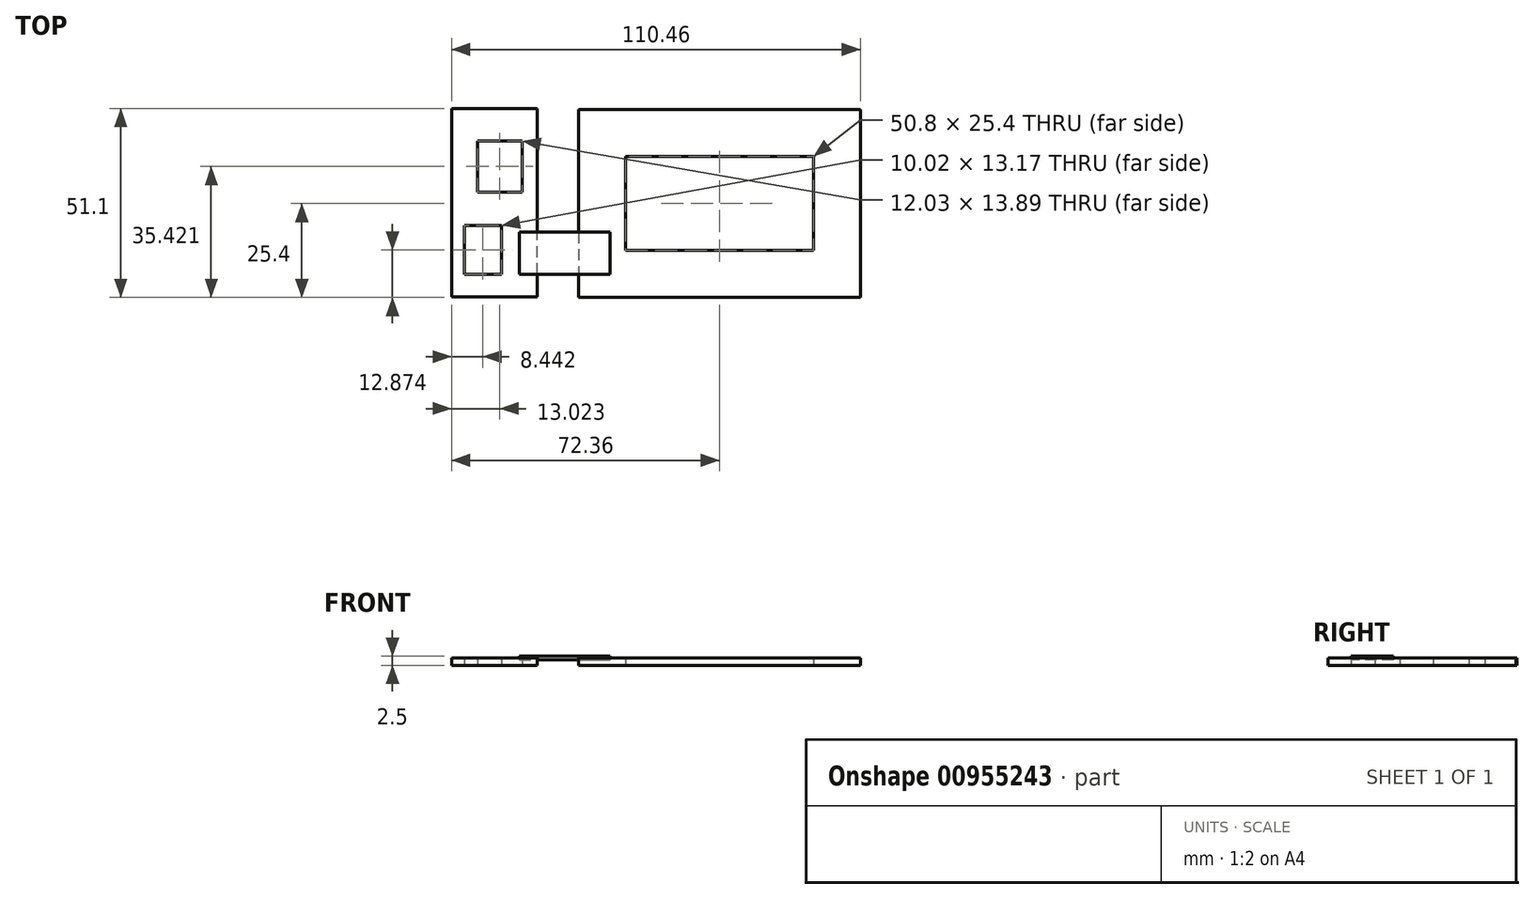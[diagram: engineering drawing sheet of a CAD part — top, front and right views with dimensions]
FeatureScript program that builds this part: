
annotation { "Feature Type Name" : "Feature", "Feature Type Description" : "" }
export const myFeature = defineFeature(function(context is Context, id is Id, definition is map)
    precondition{}
    {
        {
            var Q0;
            Q0=qCreatedBy(makeId("Top.planeOp"),FACE);
            var sketch = newSketch(context, id + "F0", { "sketchPlane" : qUnion([Q0])});
            skLineSegment(sketch, "E0.bottom", {"start": v(-38.1, 25.4) * mm, "end": v(38.1, 25.4) * mm});
            skLineSegment(sketch, "E0.top", {"start": v(-38.1, -25.4) * mm, "end": v(38.1, -25.4) * mm});
            skLineSegment(sketch, "E0.left", {"start": v(-38.1, 25.4) * mm, "end": v(-38.1, -25.4) * mm});
            skLineSegment(sketch, "E0.right", {"start": v(38.1, 25.4) * mm, "end": v(38.1, -25.4) * mm});
            skPoint(sketch, "E0.middle", {"position": v(0, 0) * mm});
            skLineSegment(sketch, "E1.bottom", {"start": v(-25.4, 12.7) * mm, "end": v(25.4, 12.7) * mm});
            skLineSegment(sketch, "E1.top", {"start": v(-25.4, -12.7) * mm, "end": v(25.4, -12.7) * mm});
            skLineSegment(sketch, "E1.left", {"start": v(-25.4, 12.7) * mm, "end": v(-25.4, -12.7) * mm});
            skLineSegment(sketch, "E1.right", {"start": v(25.4, 12.7) * mm, "end": v(25.4, -12.7) * mm});
            skLineSegment(sketch, "E2.bottom", {"start": v(-49.17, -25.27) * mm, "end": v(-72.36, -25.27) * mm});
            skLineSegment(sketch, "E2.top", {"start": v(-49.17, 25.7) * mm, "end": v(-72.36, 25.7) * mm});
            skLineSegment(sketch, "E2.left", {"start": v(-49.17, -25.27) * mm, "end": v(-49.17, 25.7) * mm});
            skLineSegment(sketch, "E2.right", {"start": v(-72.36, -25.27) * mm, "end": v(-72.36, 25.7) * mm});
            skLineSegment(sketch, "E3.bottom", {"start": v(-65.35, 16.96) * mm, "end": v(-53.32, 16.96) * mm});
            skLineSegment(sketch, "E3.top", {"start": v(-65.35, 3.08) * mm, "end": v(-53.32, 3.08) * mm});
            skLineSegment(sketch, "E3.left", {"start": v(-65.35, 16.96) * mm, "end": v(-65.35, 3.08) * mm});
            skLineSegment(sketch, "E3.right", {"start": v(-53.32, 16.96) * mm, "end": v(-53.32, 3.08) * mm});
            skLineSegment(sketch, "E4.bottom", {"start": v(-68.93, -5.94) * mm, "end": v(-58.9, -5.94) * mm});
            skLineSegment(sketch, "E4.top", {"start": v(-68.93, -19.11) * mm, "end": v(-58.9, -19.11) * mm});
            skLineSegment(sketch, "E4.left", {"start": v(-68.93, -5.94) * mm, "end": v(-68.93, -19.11) * mm});
            skLineSegment(sketch, "E4.right", {"start": v(-58.9, -5.94) * mm, "end": v(-58.9, -19.11) * mm});
            skSolve(sketch);
        }
        {
            var Q0;
            Q0 = qSketchRegion(id + "F0", true);
            extrude(context, id + "F1", {"entities" : qUnion([Q0]), "depth" : 2 * mm, "offsetDistance" : 25.4 * mm});
        }
        {
            var Q0;
            Q0=makeQuery(id+"F1.opExtrude","CAP_FACE",FACE,{"disambiguationData":[OSD([sQuery(id+"F0.wireOp",EDGE,"E2.bottom"),sQuery(id+"F0.wireOp",EDGE,"E2.top"),sQuery(id+"F0.wireOp",EDGE,"E2.left"),sQuery(id+"F0.wireOp",EDGE,"E2.right"),sQuery(id+"F0.wireOp",EDGE,"E3.bottom"),sQuery(id+"F0.wireOp",EDGE,"E3.top"),sQuery(id+"F0.wireOp",EDGE,"E3.left"),sQuery(id+"F0.wireOp",EDGE,"E3.right"),sQuery(id+"F0.wireOp",EDGE,"E4.bottom"),sQuery(id+"F0.wireOp",EDGE,"E4.top"),sQuery(id+"F0.wireOp",EDGE,"E4.left"),sQuery(id+"F0.wireOp",EDGE,"E4.right")])],"isStart":false});
            var sketch = newSketch(context, id + "F2", { "sketchPlane" : qUnion([Q0])});
            skPoint(sketch, "E5.oppositeSnap0", {"position": v(-63.92, -19.11) * mm});
            skLineSegment(sketch, "E5.bottom", {"start": v(-54.02, -7.73) * mm, "end": v(-29.54, -7.73) * mm});
            skLineSegment(sketch, "E5.top", {"start": v(-54.02, -19.11) * mm, "end": v(-29.54, -19.11) * mm});
            skLineSegment(sketch, "E5.left", {"start": v(-54.02, -7.73) * mm, "end": v(-54.02, -19.11) * mm});
            skLineSegment(sketch, "E5.right", {"start": v(-29.54, -7.73) * mm, "end": v(-29.54, -19.11) * mm});
            skSolve(sketch);
        }
        {
            var Q0;
            Q0 = qSketchRegion(id + "F2", true);
            extrude(context, id + "F3", {"entities" : qUnion([Q0]), "endBound" : BoundingType.SYMMETRIC, "depth" : 1 * mm, "offsetDistance" : 25.4 * mm});
        }
    });
